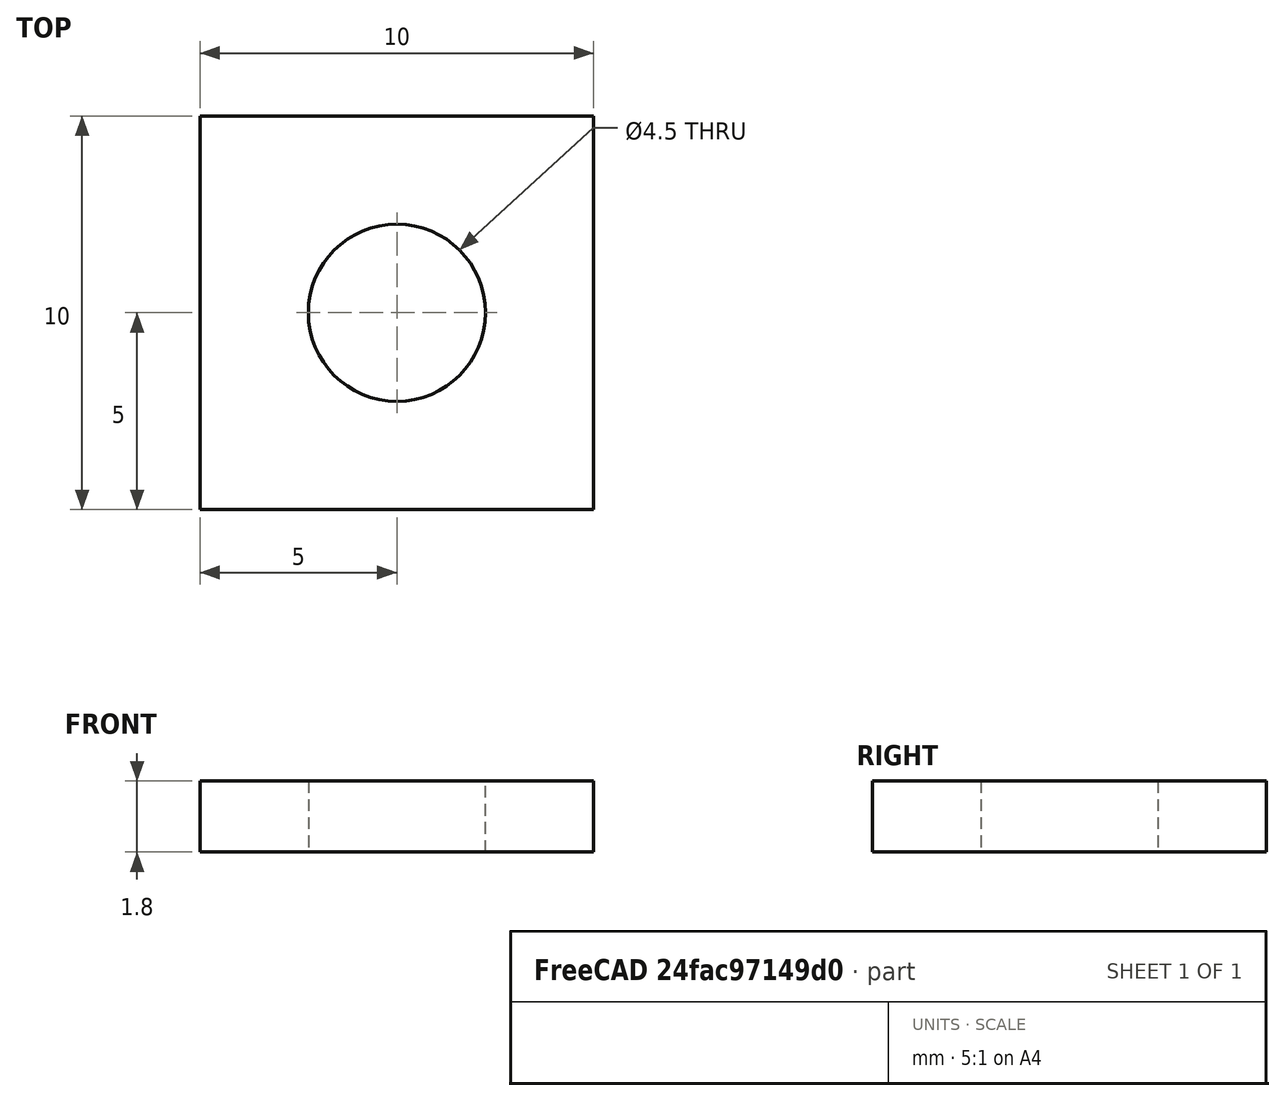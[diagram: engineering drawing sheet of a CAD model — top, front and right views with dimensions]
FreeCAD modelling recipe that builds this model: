
FCSTD DOCUMENT  (FreeCAD 1.0R39109 (Git))
Label: square_washer
License: All rights reserved
LicenseURL: http://en.wikipedia.org/wiki/All_rights_reserved
objects: Sketcher::SketchObject×1, PartDesign::Pad×1, PartDesign::Body×1
note: 6 computed .brp shape members not serialized (recipe doc carries the construction recipe); baked Part::Feature solids carry a one-line shape summary decoded from their .brp

FEATURE [Sketcher::SketchObject] Sketch
  ArcFitTolerance = 1e-06
  AttachmentSupport = -> [XY_Plane]
  FullyConstrained = true
  MakeInternals = false
  MapMode = 5
  sketch-geometry (7):
    g0: LineSegment StartX=0 StartY=0 StartZ=0 EndX=0 EndY=-10 EndZ=0
    g1: LineSegment StartX=0 StartY=-10 StartZ=0 EndX=10 EndY=-10 EndZ=0
    g2: LineSegment StartX=10 StartY=-10 StartZ=0 EndX=10 EndY=0 EndZ=0
    g3: LineSegment StartX=10 StartY=0 StartZ=0 EndX=0 EndY=0 EndZ=0
    g4: LineSegment [constr] StartX=0 StartY=0 StartZ=0 EndX=10 EndY=-10 EndZ=0
    g5: LineSegment [constr] StartX=10 StartY=0 StartZ=0 EndX=0 EndY=-10 EndZ=0
    g6: Circle CenterX=5 CenterY=-5 CenterZ=0 NormalX=0 NormalY=0 NormalZ=1 AngleXU=0 Radius=2.25
  constraints (17):
    c: Coincident(g0,g1)
    c: Coincident(g1,g2)
    c: Coincident(g2,g3)
    c: Coincident(g3,g0)
    c: Vertical(g0)
    c: Vertical(g2)
    c: Horizontal(g1)
    c: Horizontal(g3)
    c: Distance(g0,g2) = 10
    c: Distance(g1,g3) = 10
    c: Coincident(g0,g-1)
    c: Coincident(g4,g0)
    c: Coincident(g4,g1)
    c: Coincident(g5,g2)
    c: Coincident(g5,g0)
    c: Symmetric(g5,g5,g6)
    c: Diameter(g6) = 4.5
FEATURE [PartDesign::Pad] Pad
  Direction = (0,0,1)
  Length = 1.8
  Length2 = 10
  Profile = -> Sketch
  ReferenceAxis = -> Sketch [N_Axis]
  Suppressed = false
  Type = 0
FEATURE [PartDesign::Body] Body
  AllowCompound = false
  Group = -> [Sketch,Pad]
  Origin = -> Origin
  Tip = -> Pad
